# Revit family: A62_63_UN_Line Surface Mounted_ETK
name_source: partatom
category: Lighting Fixtures
units: mm (PartAtom-declared; Revit-internal decimal feet)

## family parameters
Always vertical = Yes
Cut with Voids When Loaded = No
Light Source = Yes
OmniClass Number = 23.80.70.11.14.11
OmniClass Title = Downlights
Part Type = Normal
Room Calculation Point = Yes
Round Connector Dimension = Use Diameter
Shared = No
Work Plane-Based = No

## types (1)
- A62_63_UN_Line Surface Mounted_ETK
    Apparent Load = 82 VA
    Assembly Code = 63.0
    Calc_L1_Symbol = 28 mm
    Calc_L2_Symbol = 0 mm  [stored 0 ft]
    Color Filter = 16777215
    Dimming Lamp Color Temperature Shift = <None>
    ETIM Code = ETIMCODE
    Emit Shape Visible in Rendering = No
    Emit from Rectangle Length = 41 mm  [stored 0.134514 ft]
    Emit from Rectangle Width = 2801 mm  [stored 9.18963 ft]
    GTIN Code = GTINCODE
    H1 = 82 mm  [stored 0.269029 ft]
    Housing_Material = Select RGB Value for different appearance
    IK Value = -
    IP Value = IP20
    ISBN Code = ISBNCODE
    IfcExportAs = IfcLightFixtureType
    IfcExportType = USERDEFINED
    L1 = 2805 mm  [stored 9.20276 ft]
    L2 = 45 mm  [stored 0.147638 ft]
    L3 = 2 mm  [stored 0.00656168 ft]
    L4 = 2605 mm  [stored 8.54659 ft]
    Lamp = LED
    Luminous Flux (lm) = 6346 lm
    Manufacturer = ETK B.V.
    Model = A62
    Photometric Web File = A62.2810.35_LDT.ies
    Tilt Angle = 90.00°
    Type Comments = Line Surface Mounted
    URL = www.etk.nl
    Voltage = 230 V
    Wattage Comments = 82

note: [stored X ft] marks values corroborated as IEEE doubles in the binary element streams (Revit-internal decimal feet)

## geometry (parser evidence)
native form markers: Sweep x3
no freeform markers — native parametric forms only
